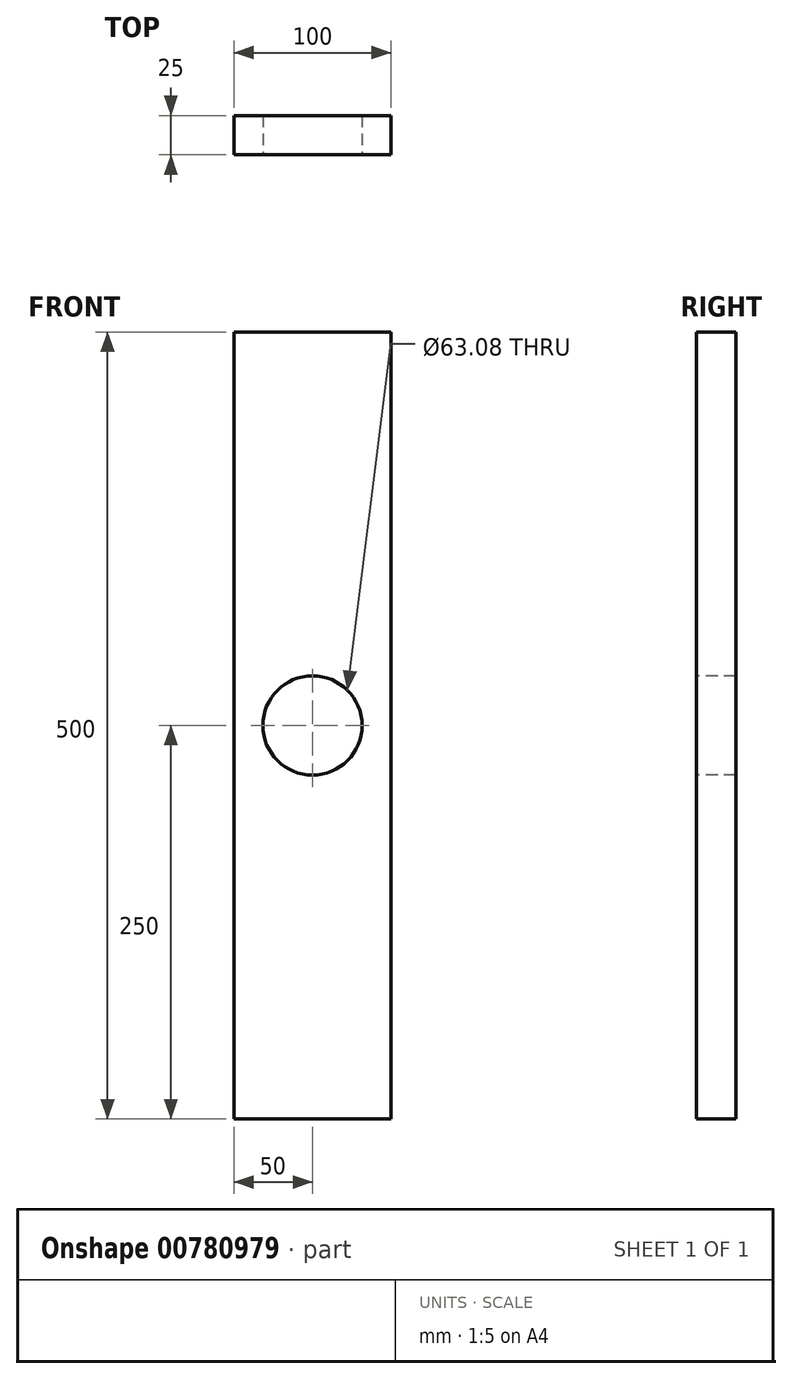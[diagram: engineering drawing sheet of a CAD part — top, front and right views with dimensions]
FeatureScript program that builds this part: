
annotation { "Feature Type Name" : "Feature", "Feature Type Description" : "" }
export const myFeature = defineFeature(function(context is Context, id is Id, definition is map)
    precondition{}
    {
        {
            var Q0;
            Q0=qCreatedBy(makeId("Front.planeOp"),FACE);
            var sketch = newSketch(context, id + "F0", { "sketchPlane" : qUnion([Q0])});
            skLineSegment(sketch, "E0", {"start": v(-50, 250) * mm, "end": v(-50, -250) * mm});
            skLineSegment(sketch, "E1", {"start": v(-50, -250) * mm, "end": v(50, -250) * mm});
            skLineSegment(sketch, "E2", {"start": v(50, -250) * mm, "end": v(50, 250) * mm});
            skLineSegment(sketch, "E3", {"start": v(50, 250) * mm, "end": v(-50, 250) * mm});
            skSolve(sketch);
        }
        {
            var Q0;
            Q0 = qSketchRegion(id + "F0", true);
            extrude(context, id + "F1", {"entities" : qUnion([Q0]), "endBound" : BoundingType.SYMMETRIC, "depth" : 25 * mm, "offsetDistance" : 25 * mm});
        }
        {
            var Q0;
            Q0=makeQuery(id+"F1.opExtrude","CAP_FACE",FACE,{"disambiguationData":[OSD([sQuery(id+"F0.wireOp",EDGE,"E0"),sQuery(id+"F0.wireOp",EDGE,"E1"),sQuery(id+"F0.wireOp",EDGE,"E2"),sQuery(id+"F0.wireOp",EDGE,"E3")])],"isStart":false});
            var sketch = newSketch(context, id + "F2", { "sketchPlane" : qUnion([Q0])});
            skPoint(sketch, "E4", {"position": v(0, 0) * mm});
            skCircle(sketch, "E5", {"center": v(0, 0) * mm, "radius": 31.54 * mm});
            skSolve(sketch);
        }
        {
            var Q0;
            Q0 = qSketchRegion(id + "F2", true);
            extrude(context, id + "F3", {"entities" : qUnion([Q0]), "operationType" : NewBodyOperationType.REMOVE, "oppositeDirection" : true, "depth" : 25 * mm, "offsetDistance" : 25 * mm});
        }
    });
